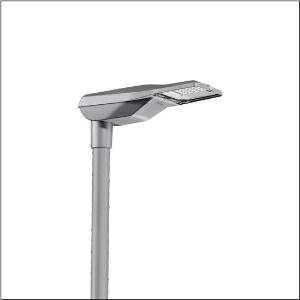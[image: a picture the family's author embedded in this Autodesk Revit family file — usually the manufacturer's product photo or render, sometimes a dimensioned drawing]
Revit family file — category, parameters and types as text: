
# Revit family: streetlight_sl_21_iq_micro___p0_8a_5xe1u31g08cb_6469
name_source: partatom
category: Lighting Fixtures
units: mm (PartAtom-declared; Revit-internal decimal feet)

## family parameters
Cut with Voids When Loaded = No
Host = Face
Light Source = No
Part Type = Normal
Room Calculation Point = No
Round Connector Dimension = Use Diameter
Shared = No

## types (1)
- --- (1 x LED, 2830 lm, 19.4 W, 3000K)
    Apparent Load = 19 VA
    CIE Flux Codes = 33 69 96 100 100
    Color Rendering = 70
    Color Temperature = 3000K
    Default Elevation = 1800 mm
    Description = Streetlight SL 21 iQ micro, mast luminaire, primary light control with lens, of PMMA, primary optical cover: cover, of toughened safety glass, transparent, light distribution: P0.8a, light emission: direct distribution, primary light characteristic: asymmetric, installation type: post-top, side-entry, LED, High Power LED, rated luminous flux: 2.830lm, luminous efficacy: 146lm/W, light colour: 730, colour temperature: 3000K, control gear: iQ Street-Remote, control: pre-setting: linear dimming characteristic, Street-Remote, Auto-Match, Temp-Guard, Lumen-Switch, Night-Set, Smart-Wire, Light-Fading, Desk-Remote (wireless, voltage-free reading and setting of iQ features in the workshop via application-optimized NFC function/RFID function), optimised constant luminous flux control (CLO 2.0), mains connection: 220..240V, AC, 50/60Hz, start of lifetime: 19W, end of service life: 20W, reduction: 10W, luminaire housing, of diecast aluminium, powder-coated, Siteco® metallic grey (DB 702S), corrosivity category C5 high according to DIN EN ISO 12944, please order mast flange separately, inclination adjustable: 0°, 5°, 10°, 15°, sealing non-destructively replaceable, multi-level sealing system, length: 528mm, width: 235mm, height: 110mm, mast flange for spigot size: 42mm (side-entry): 5XC10008XM4, 60/48mm (side-entry/post-top): 5XC10108XM2, 76/60mm (side-entry/post-top): 5XC10108XM1, protection rating (complete): IP66, insulation class (complete): insulation class II (safety insulation), certification: CE, ENEC, ENEC+, VDE, impact resistance: IK10, permissible operating ambient temperature for outdoor applications: -40..+50°C, standard-compliant lighting for roads and squares, packaging unit: 1 piece

Light Distribution: P0.8a
    Height = 110 mm
    Lamp = 1 x LED
    Lamp Light Flux = 2830 lm
    Lamp Power = 19.4 W
    Lamp count = 1
    Length = 528 mm
    Luminous efficacy = 146 lm/W
    Manufacturer = Siteco
    ModVariant = No
    Model = 5XE1U31G08CB
    Number of Poles = 1
    OnlyDefault = Yes
    Power Factor = 1
    Product Name = Streetlight SL 21 iQ micro | P0.8a
    Product group = mast luminaire | pylon top
    ProductGroupID = 6100
    Protection Class = Protection class II
    Protection Degree = IP 66
    RLX_Detail_Level = 1
    RLX_Emergency_Light_Flux = 0 lm
    RLX_Emergency_Type = 0
    RLX_Emergency_Type_DB = No
    RlxData = <blob elided: 98969 chars, md5=543fb465>
    Socket = socket
    Standby Power = 0 W
    System Light Flux = 2830 lm
    System Power = 19 W
    Type Comments = factory setting: luminous flux: 100 % | dim-lin: 254 | 387 mA
    Type Image = l_1006881.jpg
    URL = http://relux.com
    VarID = @adj_083423
    Voltage = 0 V
    Weight = 0.00 kg
    Width = 235 mm

## geometry (parser evidence)
native form markers: Blend x4, Sweep x8
no freeform markers — native parametric forms only
